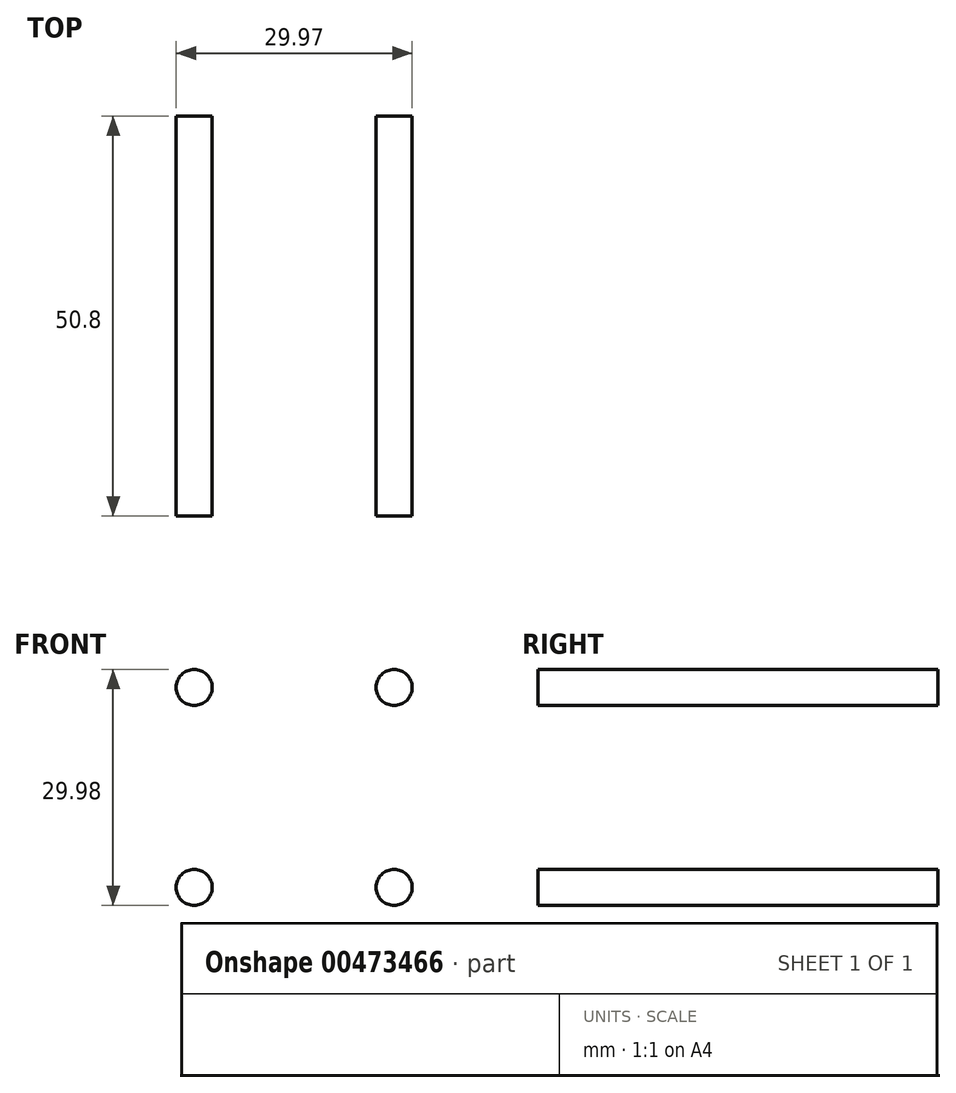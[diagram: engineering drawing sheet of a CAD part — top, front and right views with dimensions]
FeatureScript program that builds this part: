
annotation { "Feature Type Name" : "Feature", "Feature Type Description" : "" }
export const myFeature = defineFeature(function(context is Context, id is Id, definition is map)
    precondition{}
    {
        {
            var Q0;
            Q0=qCreatedBy(makeId("Front.planeOp"),FACE);
            var sketch = newSketch(context, id + "F0", { "sketchPlane" : qUnion([Q0])});
            skCircle(sketch, "E0", {"center": v(-34.95, 20.5) * mm, "radius": 2.29 * mm});
            skCircle(sketch, "E1.0.1.0", {"center": v(-34.95, 45.9) * mm, "radius": 2.29 * mm});
            skCircle(sketch, "E1.1.0.0", {"center": v(-9.55, 20.5) * mm, "radius": 2.29 * mm});
            skCircle(sketch, "E1.1.1.0", {"center": v(-9.55, 45.9) * mm, "radius": 2.29 * mm});
            skLineSegment(sketch, "E1.direction1", {"start": v(-34.95, 20.5) * mm, "end": v(-9.55, 20.5) * mm, "construction": true});
            skLineSegment(sketch, "E1.direction2", {"start": v(-34.95, 20.5) * mm, "end": v(-34.95, 45.9) * mm, "construction": true});
            skSolve(sketch);
        }
        {
            var Q0;
            Q0=makeQuery(id+"F0.imprint","IMPRINT",FACE,{"disambiguationData":[TD([[makeQuery(id+"F0.imprint","IMPRINT",EDGE,{"derivedFrom":sQuery(id+"F0.wireOp",EDGE,"E1.0.1.0")}),1.0]])]});
            var Q1;
            Q1=makeQuery(id+"F0.imprint","IMPRINT",FACE,{"disambiguationData":[TD([[makeQuery(id+"F0.imprint","IMPRINT",EDGE,{"derivedFrom":sQuery(id+"F0.wireOp",EDGE,"E1.1.1.0")}),1.0]])]});
            var Q2;
            Q2=makeQuery(id+"F0.imprint","IMPRINT",FACE,{"disambiguationData":[TD([[makeQuery(id+"F0.imprint","IMPRINT",EDGE,{"derivedFrom":sQuery(id+"F0.wireOp",EDGE,"E1.1.0.0")}),1.0]])]});
            var Q3;
            Q3=makeQuery(id+"F0.imprint","IMPRINT",FACE,{"disambiguationData":[TD([[makeQuery(id+"F0.imprint","IMPRINT",EDGE,{"derivedFrom":sQuery(id+"F0.wireOp",EDGE,"E0")}),1.0]])]});
            extrude(context, id + "F1", {"entities" : qUnion([Q0, Q1, Q2, Q3]), "depth" : 50.8 * mm});
        }
    });
